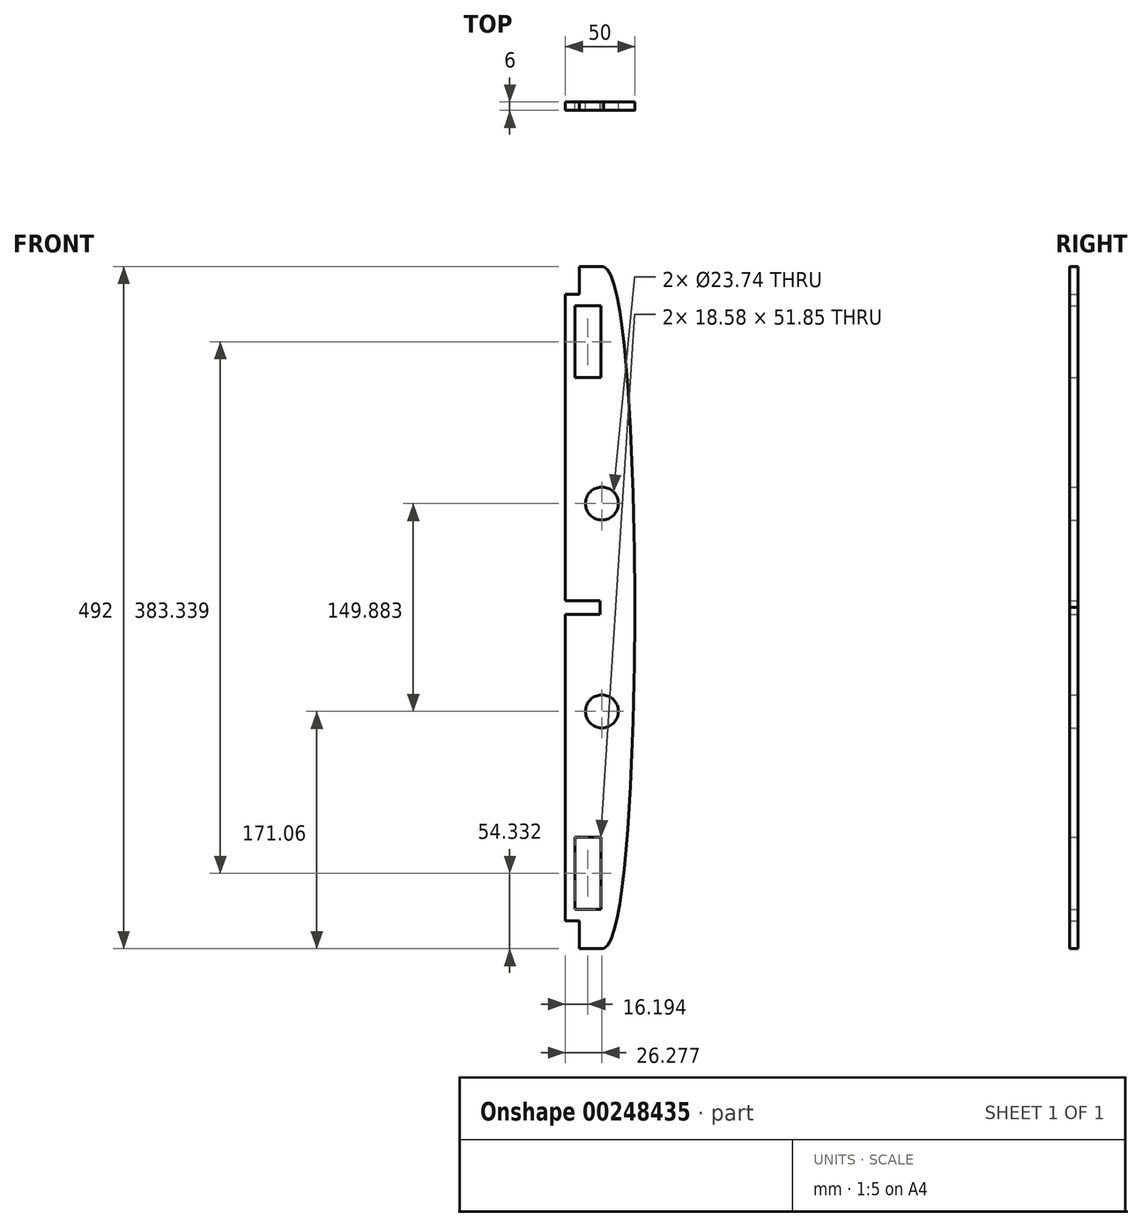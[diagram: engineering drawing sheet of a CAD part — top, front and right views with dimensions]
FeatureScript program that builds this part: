
annotation { "Feature Type Name" : "Feature", "Feature Type Description" : "" }
export const myFeature = defineFeature(function(context is Context, id is Id, definition is map)
    precondition{}
    {
        {
            var Q0;
            Q0=qCreatedBy(makeId("Front.planeOp"),FACE);
            var sketch = newSketch(context, id + "F0", { "sketchPlane" : qUnion([Q0])});
            skFitSpline(sketch, "E0", {"points": [v(192.75, 203.85) * mm, v(215.25, -42.15) * mm], "startDerivative": vector(67.6, -22.2) * mm, "endDerivative": vector(-0.1, -5.55) * mm});
            skLineSegment(sketch, "E1", {"start": v(215.25, -42.15) * mm, "end": v(165.25, -42.15) * mm});
            skLineSegment(sketch, "E2", {"start": v(215.28, 203.85) * mm, "end": v(215.28, -40.3) * mm});
            skLineSegment(sketch, "E3.bottom", {"start": v(190.73, 175.44) * mm, "end": v(172.16, 175.44) * mm});
            skLineSegment(sketch, "E3.top", {"start": v(190.73, 123.6) * mm, "end": v(172.16, 123.6) * mm});
            skLineSegment(sketch, "E3.left", {"start": v(190.73, 175.44) * mm, "end": v(190.73, 123.6) * mm});
            skLineSegment(sketch, "E3.right", {"start": v(172.16, 175.44) * mm, "end": v(172.16, 123.6) * mm});
            skCircle(sketch, "E4", {"center": v(191.53, 32.8) * mm, "radius": 11.87 * mm});
            skLineSegment(sketch, "E5.MirrorCS", {"start": v(190.73, -207.9) * mm, "end": v(172.16, -207.9) * mm});
            skLineSegment(sketch, "E6.MirrorCS", {"start": v(172.16, -259.74) * mm, "end": v(172.16, -207.9) * mm});
            skFitSpline(sketch, "E7.MirrorCS", {"points": [v(192.75, -288.15) * mm, v(215.25, -42.15) * mm], "startDerivative": vector(67.6, 22.2) * mm, "endDerivative": vector(-0.1, 5.55) * mm});
            skLineSegment(sketch, "E8.MirrorCS", {"start": v(215.28, -288.15) * mm, "end": v(175.25, -288.15) * mm});
            skLineSegment(sketch, "E9.MirrorCS", {"start": v(215.28, -288.15) * mm, "end": v(215.28, -44) * mm});
            skLineSegment(sketch, "E10.MirrorCS", {"start": v(190.73, -259.74) * mm, "end": v(172.16, -259.74) * mm});
            skLineSegment(sketch, "E11.MirrorCS", {"start": v(190.73, -259.74) * mm, "end": v(190.73, -207.9) * mm});
            skCircle(sketch, "E12.MirrorC", {"center": v(191.53, -117.1) * mm, "radius": 11.87 * mm});
            skLineSegment(sketch, "E13", {"start": v(190.25, -42.15) * mm, "end": v(190.25, -47.15) * mm});
            skLineSegment(sketch, "E14", {"start": v(190.25, -42.15) * mm, "end": v(190.25, -37.15) * mm});
            skLineSegment(sketch, "E15", {"start": v(190.25, -37.15) * mm, "end": v(165.25, -37.15) * mm});
            skLineSegment(sketch, "E16", {"start": v(190.25, -47.15) * mm, "end": v(165.25, -47.15) * mm});
            skLineSegment(sketch, "E17", {"start": v(175.25, 203.85) * mm, "end": v(175.25, 183.85) * mm});
            skLineSegment(sketch, "E18", {"start": v(175.25, 183.85) * mm, "end": v(165.25, 183.85) * mm});
            skLineSegment(sketch, "E19", {"start": v(175.25, 203.85) * mm, "end": v(192.75, 203.85) * mm});
            skLineSegment(sketch, "E20", {"start": v(165.25, 183.85) * mm, "end": v(165.25, -42.15) * mm});
            skLineSegment(sketch, "E21", {"start": v(192.75, 203.85) * mm, "end": v(215.28, 203.85) * mm});
            skLineSegment(sketch, "E22.MirrorCS", {"start": v(175.25, -288.15) * mm, "end": v(175.25, -268.15) * mm});
            skLineSegment(sketch, "E23.MirrorCS", {"start": v(175.25, -268.15) * mm, "end": v(165.25, -268.15) * mm});
            skLineSegment(sketch, "E24", {"start": v(175.25, -288.15) * mm, "end": v(175.25, -288.15) * mm});
            skLineSegment(sketch, "E25", {"start": v(165.25, -268.15) * mm, "end": v(165.25, -42.15) * mm});
            skLineSegment(sketch, "E26", {"start": v(165.25, -268.15) * mm, "end": v(165.25, -268.15) * mm});
            skSolve(sketch);
        }
        {
            var Q0;
            Q0=makeQuery(id+"F0.imprint","IMPRINT",FACE,{"disambiguationData":[TD([[makeQuery(id+"F0.imprint","IMPRINT",EDGE,{"derivedFrom":sQuery(id+"F0.wireOp",EDGE,"7156f876-30db-4834-be3f-2c649fc2f715")}),-1.0]])]});
            var Q1;
            Q1=makeQuery(id+"F0.imprint","IMPRINT",FACE,{"disambiguationData":[TD([[makeQuery(id+"F0.imprint","IMPRINT",EDGE,{"derivedFrom":sQuery(id+"F0.wireOp",EDGE,"E5.MirrorCS")}),-1.0]])]});
            var Q2;
            {var subQ0=sQuery(id+"F0.wireOp",EDGE,"E0");Q2=makeQuery(id+"F0.imprint","IMPRINT",FACE,{"disambiguationData":[TD([[makeQuery(id+"F0.imprint","IMPRINT",EDGE,{"derivedFrom":subQ0}),-1.0]])]});}
            extrude(context, id + "F1", {"entities" : qUnion([Q0, Q1, Q2]), "depth" : 6 * mm});
        }
    });
